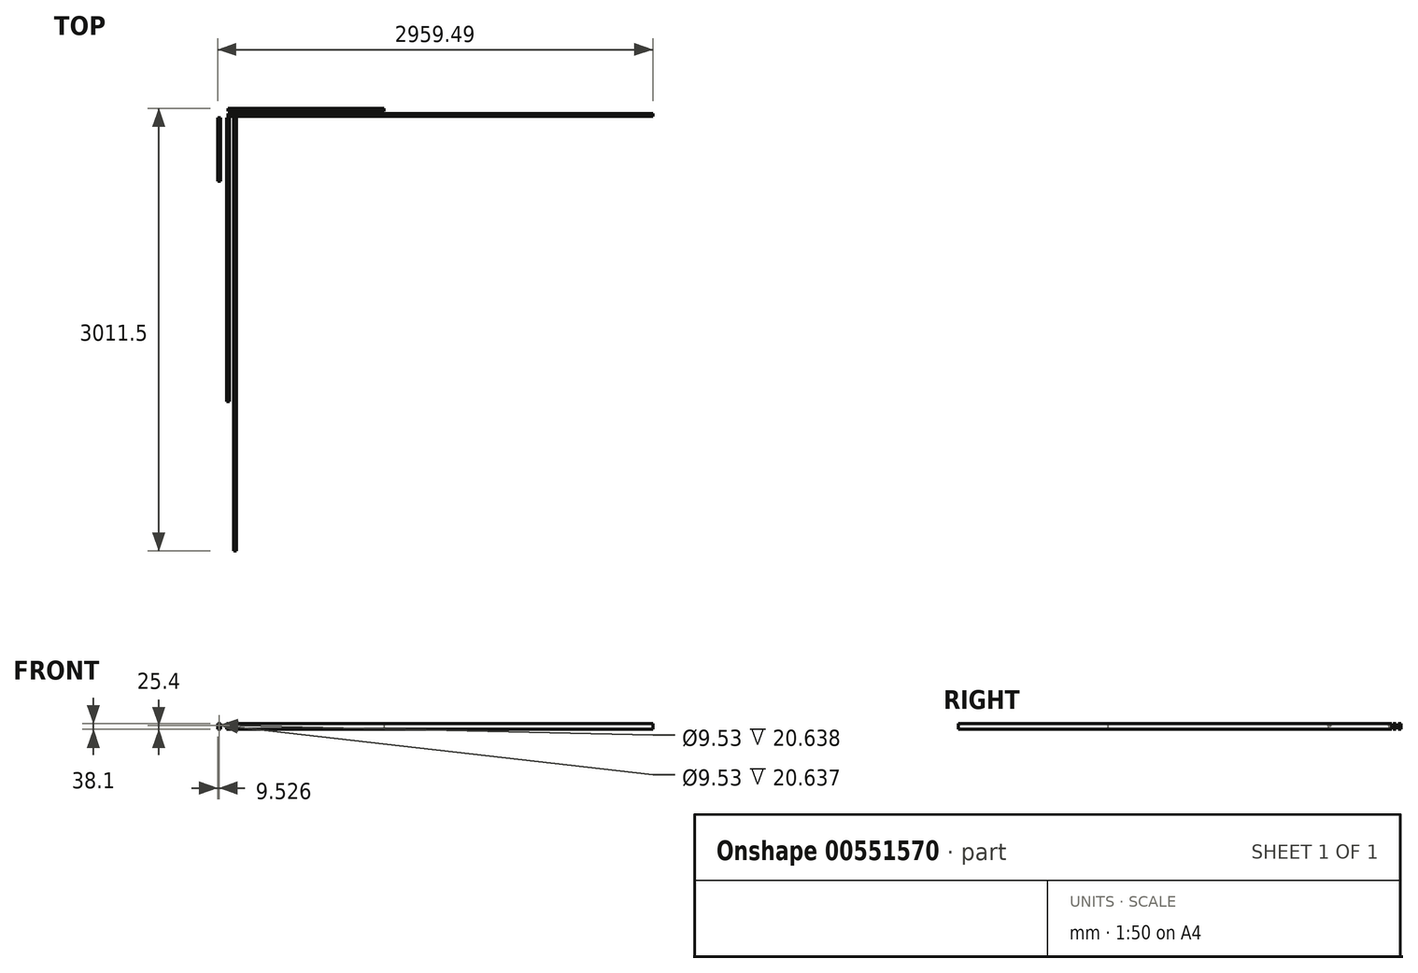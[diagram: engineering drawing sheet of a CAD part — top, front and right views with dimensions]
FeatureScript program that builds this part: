
annotation { "Feature Type Name" : "Feature", "Feature Type Description" : "" }
export const myFeature = defineFeature(function(context is Context, id is Id, definition is map)
    precondition{}
    {
        {
            var Q0;
            Q0=qCreatedBy(makeId("Front.planeOp"),FACE);
            var sketch = newSketch(context, id + "F0", { "sketchPlane" : qUnion([Q0])});
            skLineSegment(sketch, "E0.bottom", {"start": v(-51.19, 19.05) * mm, "end": v(-70.24, 19.05) * mm});
            skLineSegment(sketch, "E0.top", {"start": v(-51.19, -19.05) * mm, "end": v(-70.24, -19.05) * mm});
            skLineSegment(sketch, "E0.left", {"start": v(-51.19, 19.05) * mm, "end": v(-51.19, -19.05) * mm});
            skLineSegment(sketch, "E0.right", {"start": v(-70.24, 19.05) * mm, "end": v(-70.24, -19.05) * mm});
            skPoint(sketch, "E0.middle", {"position": v(-60.71, 0) * mm});
            skSolve(sketch);
        }
        {
            var Q0;
            Q0=qCreatedBy(makeId("Front.planeOp"),FACE);
            var sketch = newSketch(context, id + "F1", { "sketchPlane" : qUnion([Q0])});
            skLineSegment(sketch, "E1.bottom", {"start": v(9.53, 19.05) * mm, "end": v(-9.52, 19.05) * mm});
            skLineSegment(sketch, "E1.top", {"start": v(9.52, -19.05) * mm, "end": v(-9.53, -19.05) * mm});
            skLineSegment(sketch, "E1.left", {"start": v(9.53, 19.05) * mm, "end": v(9.52, -19.05) * mm});
            skLineSegment(sketch, "E1.right", {"start": v(-9.52, 19.05) * mm, "end": v(-9.53, -19.05) * mm});
            skPoint(sketch, "E1.middle", {"position": v(0, 0) * mm});
            skSolve(sketch);
        }
        {
            var Q0;
            Q0=qCreatedBy(makeId("Front.planeOp"),FACE);
            var sketch = newSketch(context, id + "F2", { "sketchPlane" : qUnion([Q0])});
            skLineSegment(sketch, "E2.bottom", {"start": v(57.69, 19.05) * mm, "end": v(38.64, 19.05) * mm});
            skLineSegment(sketch, "E2.top", {"start": v(57.69, -19.05) * mm, "end": v(38.64, -19.05) * mm});
            skLineSegment(sketch, "E2.left", {"start": v(57.69, 19.05) * mm, "end": v(57.69, -19.05) * mm});
            skLineSegment(sketch, "E2.right", {"start": v(38.64, 19.05) * mm, "end": v(38.64, -19.05) * mm});
            skPoint(sketch, "E2.middle", {"position": v(48.16, 0) * mm});
            skSolve(sketch);
        }
        {
            var Q0;
            Q0=makeQuery(id+"F0.imprint","IMPRINT",FACE,{"disambiguationData":[TD([[makeQuery(id+"F0.imprint","IMPRINT",EDGE,{"derivedFrom":sQuery(id+"F0.wireOp",EDGE,"E0.bottom")}),1.0]])]});
            extrude(context, id + "F3", {"entities" : qUnion([Q0]), "depth" : 431.8 * mm, "offsetDistance" : 25.4 * mm});
        }
        {
            var Q0;
            Q0=makeQuery(id+"F1.imprint","IMPRINT",FACE,{"disambiguationData":[TD([[makeQuery(id+"F1.imprint","IMPRINT",EDGE,{"derivedFrom":sQuery(id+"F1.wireOp",EDGE,"E1.bottom")}),1.0]])]});
            extrude(context, id + "F4", {"entities" : qUnion([Q0]), "depth" : 1930.4 * mm, "offsetDistance" : 25.4 * mm});
        }
        {
            var Q0;
            Q0=makeQuery(id+"F2.imprint","IMPRINT",FACE,{"disambiguationData":[TD([[makeQuery(id+"F2.imprint","IMPRINT",EDGE,{"derivedFrom":sQuery(id+"F2.wireOp",EDGE,"E2.bottom")}),1.0]])]});
            extrude(context, id + "F5", {"entities" : qUnion([Q0]), "depth" : 2946.4 * mm, "offsetDistance" : 25.4 * mm});
        }
        {
            var Q0;
            Q0=qCreatedBy(makeId("Right.planeOp"),FACE);
            var sketch = newSketch(context, id + "F6", { "sketchPlane" : qUnion([Q0])});
            skLineSegment(sketch, "E3.bottom", {"start": v(30.39, 19.05) * mm, "end": v(11.34, 19.05) * mm});
            skLineSegment(sketch, "E3.top", {"start": v(30.39, -19.05) * mm, "end": v(11.34, -19.05) * mm});
            skLineSegment(sketch, "E3.left", {"start": v(30.39, 19.05) * mm, "end": v(30.39, -19.05) * mm});
            skLineSegment(sketch, "E3.right", {"start": v(11.34, 19.05) * mm, "end": v(11.34, -19.05) * mm});
            skPoint(sketch, "E3.middle", {"position": v(20.86, 0) * mm});
            skSolve(sketch);
        }
        {
            var Q0;
            Q0=qCreatedBy(makeId("Right.planeOp"),FACE);
            var sketch = newSketch(context, id + "F7", { "sketchPlane" : qUnion([Q0])});
            skLineSegment(sketch, "E4.bottom", {"start": v(65.1, 19.05) * mm, "end": v(46.05, 19.05) * mm});
            skLineSegment(sketch, "E4.top", {"start": v(65.1, -19.05) * mm, "end": v(46.05, -19.05) * mm});
            skLineSegment(sketch, "E4.left", {"start": v(65.1, 19.05) * mm, "end": v(65.1, -19.05) * mm});
            skLineSegment(sketch, "E4.right", {"start": v(46.05, 19.05) * mm, "end": v(46.05, -19.05) * mm});
            skPoint(sketch, "E4.middle", {"position": v(55.58, 0) * mm});
            skSolve(sketch);
        }
        {
            var Q0;
            Q0 = qSketchRegion(id + "F6", true);
            extrude(context, id + "F8", {"entities" : qUnion([Q0]), "depth" : 2889.25 * mm, "offsetDistance" : 25.4 * mm});
        }
        {
            var Q0;
            Q0=makeQuery(id+"F7.imprint","IMPRINT",FACE,{"disambiguationData":[TD([[makeQuery(id+"F7.imprint","IMPRINT",EDGE,{"derivedFrom":sQuery(id+"F7.wireOp",EDGE,"E4.bottom")}),1.0]])]});
            extrude(context, id + "F9", {"entities" : qUnion([Q0]), "depth" : 1060.45 * mm, "offsetDistance" : 25.4 * mm});
        }
        {
            var Q0;
            Q0=makeQuery(id+"F3.opExtrude","CAP_FACE",FACE,{"disambiguationData":[OSD([sQuery(id+"F0.wireOp",EDGE,"E0.bottom"),sQuery(id+"F0.wireOp",EDGE,"E0.top"),sQuery(id+"F0.wireOp",EDGE,"E0.left"),sQuery(id+"F0.wireOp",EDGE,"E0.right")])],"isStart":false});
            var sketch = newSketch(context, id + "F10", { "sketchPlane" : qUnion([Q0])});
            skCircle(sketch, "E5", {"center": v(-60.71, 6.35) * mm, "radius": 4.76 * mm});
            skSolve(sketch);
        }
        {
            var Q0;
            Q0=makeQuery(id+"F10.imprint","IMPRINT",FACE,{"disambiguationData":[TD([[makeQuery(id+"F10.imprint","IMPRINT",EDGE,{"derivedFrom":sQuery(id+"F10.wireOp",EDGE,"E5")}),1.0]])]});
            extrude(context, id + "F11", {"entities" : qUnion([Q0]), "operationType" : NewBodyOperationType.REMOVE, "oppositeDirection" : true, "depth" : 20.64 * mm, "offsetDistance" : 25.4 * mm});
        }
        {
            var Q0;
            Q0=makeQuery(id+"F3.opExtrude","CAP_FACE",FACE,{"disambiguationData":[OSD([sQuery(id+"F0.wireOp",EDGE,"E0.bottom"),sQuery(id+"F0.wireOp",EDGE,"E0.top"),sQuery(id+"F0.wireOp",EDGE,"E0.left"),sQuery(id+"F0.wireOp",EDGE,"E0.right")])],"isStart":true});
            var sketch = newSketch(context, id + "F12", { "sketchPlane" : qUnion([Q0])});
            skCircle(sketch, "E6", {"center": v(60.71, 6.35) * mm, "radius": 4.76 * mm});
            skSolve(sketch);
        }
        {
            var Q0;
            Q0=makeQuery(id+"F12.imprint","IMPRINT",FACE,{"disambiguationData":[TD([[makeQuery(id+"F12.imprint","IMPRINT",EDGE,{"derivedFrom":sQuery(id+"F12.wireOp",EDGE,"E6")}),1.0]])]});
            extrude(context, id + "F13", {"entities" : qUnion([Q0]), "operationType" : NewBodyOperationType.REMOVE, "oppositeDirection" : true, "depth" : 20.64 * mm, "offsetDistance" : 25.4 * mm});
        }
    });
